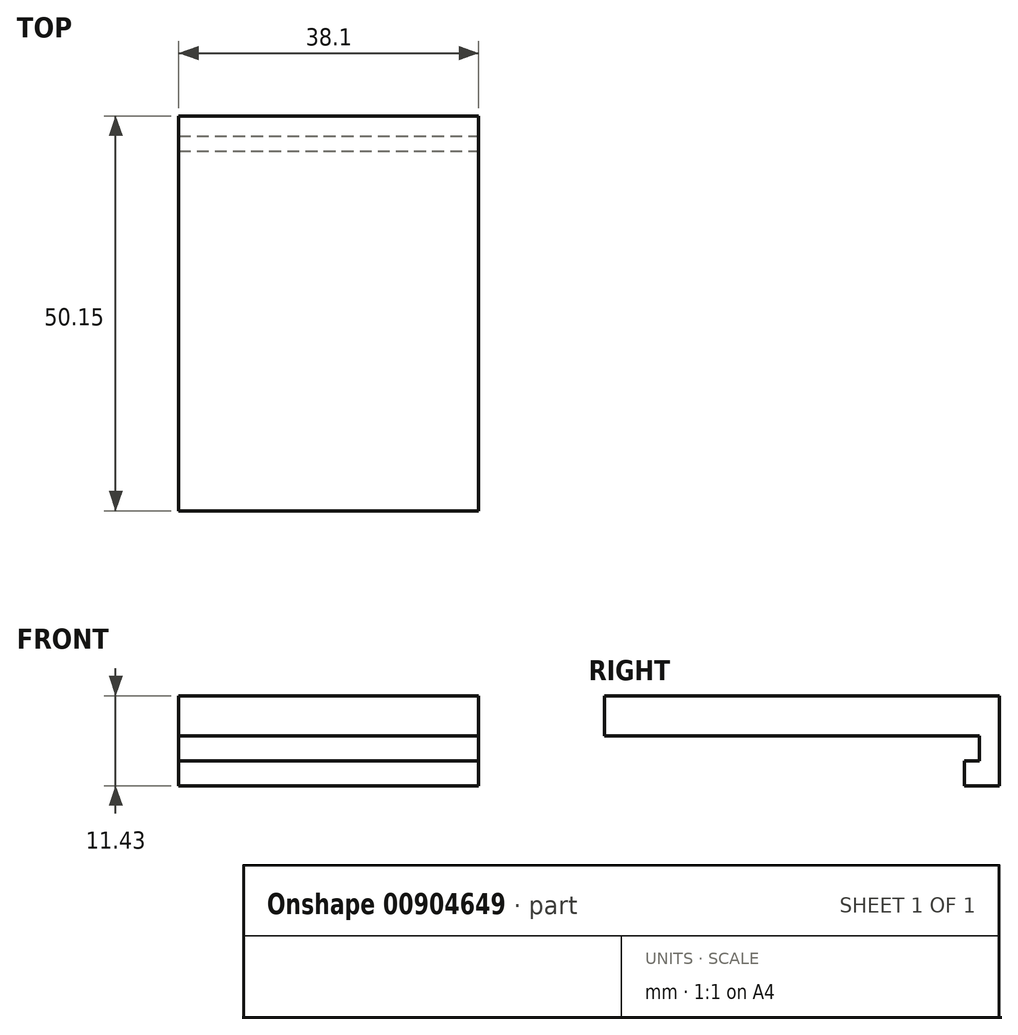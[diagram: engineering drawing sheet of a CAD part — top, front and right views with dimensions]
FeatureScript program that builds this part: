
annotation { "Feature Type Name" : "Feature", "Feature Type Description" : "" }
export const myFeature = defineFeature(function(context is Context, id is Id, definition is map)
    precondition{}
    {
        {
            var Q0;
            Q0=qCreatedBy(makeId("Top.planeOp"),FACE);
            var sketch = newSketch(context, id + "F0", { "sketchPlane" : qUnion([Q0])});
            skLineSegment(sketch, "E0.bottom", {"start": v(19.05, 12.7) * mm, "end": v(-19.05, 12.7) * mm});
            skLineSegment(sketch, "E0.top", {"start": v(19.05, -12.7) * mm, "end": v(-19.05, -12.7) * mm});
            skLineSegment(sketch, "E0.left", {"start": v(19.05, 12.7) * mm, "end": v(19.05, -12.7) * mm});
            skLineSegment(sketch, "E0.right", {"start": v(-19.05, 12.7) * mm, "end": v(-19.05, -12.7) * mm});
            skPoint(sketch, "E0.middle", {"position": v(0, 0) * mm});
            skSolve(sketch);
        }
        {
            var Q0;
            Q0=makeQuery(id+"F0.imprint","IMPRINT",FACE,{"disambiguationData":[TD([[makeQuery(id+"F0.imprint","IMPRINT",EDGE,{"derivedFrom":sQuery(id+"F0.wireOp",EDGE,"E0.bottom")}),1.0]])]});
            extrude(context, id + "F1", {"entities" : qUnion([Q0]), "depth" : 5.08 * mm, "offsetDistance" : 25.4 * mm});
        }
        {
            var Q0;
            Q0=makeQuery(id+"F1.opExtrude","SWEPT_FACE",FACE,{"disambiguationData":[OSD([sQuery(id+"F0.wireOp",EDGE,"E0.bottom")])]});
            var sketch = newSketch(context, id + "F2", { "sketchPlane" : qUnion([Q0])});
            skLineSegment(sketch, "E1.bottom", {"start": v(-19.05, 5.08) * mm, "end": v(19.05, 5.08) * mm});
            skLineSegment(sketch, "E1.top", {"start": v(-19.05, 0) * mm, "end": v(19.05, 0) * mm});
            skLineSegment(sketch, "E1.left", {"start": v(-19.05, 5.08) * mm, "end": v(-19.05, 0) * mm});
            skLineSegment(sketch, "E1.right", {"start": v(19.05, 5.08) * mm, "end": v(19.05, 0) * mm});
            skSolve(sketch);
        }
        {
            var Q0;
            Q0=makeQuery(id+"F2.imprint","IMPRINT",FACE,{"disambiguationData":[TD([[makeQuery(id+"F2.imprint","IMPRINT",EDGE,{"derivedFrom":sQuery(id+"F2.wireOp",EDGE,"E1.bottom")}),-1.0]])]});
            extrude(context, id + "F3", {"entities" : qUnion([Q0]), "operationType" : NewBodyOperationType.ADD, "depth" : 22.22 * mm, "offsetDistance" : 25.4 * mm});
        }
        {
            var Q0;
            Q0=makeQuery(id+"F3.boolean.opBoolean","MERGE",FACE,{"derivedFrom":[makeQuery(id+"F1.opExtrude","SWEPT_FACE",FACE,{"disambiguationData":[OSD([sQuery(id+"F0.wireOp",EDGE,"E0.right")])]}),makeQuery(id+"F3.opExtrude","SWEPT_FACE",FACE,{"disambiguationData":[OSD([sQuery(id+"F2.wireOp",EDGE,"E1.right")])]})]});
            var sketch = newSketch(context, id + "F4", { "sketchPlane" : qUnion([Q0])});
            skLineSegment(sketch, "E2", {"start": v(-34.92, 5.08) * mm, "end": v(-37.45, 5.08) * mm});
            skLineSegment(sketch, "E3", {"start": v(-34.92, 0) * mm, "end": v(-37.45, 0) * mm});
            skLineSegment(sketch, "E4", {"start": v(-37.45, 0) * mm, "end": v(-37.45, 5.08) * mm});
            skSolve(sketch);
        }
        {
            var Q0;
            Q0=makeQuery(id+"F4.imprint","IMPRINT",FACE,{"disambiguationData":[TD([[makeQuery(id+"F4.imprint","IMPRINT",EDGE,{"derivedFrom":sQuery(id+"F4.wireOp",EDGE,"E2")}),1.0]])]});
            extrude(context, id + "F5", {"entities" : qUnion([Q0]), "operationType" : NewBodyOperationType.ADD, "depth" : -38.1 * mm, "offsetDistance" : 25.4 * mm});
        }
        {
            var Q0;
            Q0=makeQuery(id+"F5.boolean.opBoolean","MERGE",FACE,{"derivedFrom":[makeQuery(id+"F3.opExtrude","SWEPT_FACE",FACE,{"disambiguationData":[OSD([sQuery(id+"F2.wireOp",EDGE,"E1.top")])]}),makeQuery(id+"F5.opExtrude","SWEPT_FACE",FACE,{"disambiguationData":[OSD([sQuery(id+"F4.wireOp",EDGE,"E3")])]})]});
            var sketch = newSketch(context, id + "F6", { "sketchPlane" : qUnion([Q0])});
            skLineSegment(sketch, "E5.bottom", {"start": v(-19.05, -37.45) * mm, "end": v(19.05, -37.45) * mm});
            skLineSegment(sketch, "E5.top", {"start": v(-19.05, -34.91) * mm, "end": v(19.05, -34.91) * mm});
            skLineSegment(sketch, "E5.left", {"start": v(-19.05, -37.45) * mm, "end": v(-19.05, -34.91) * mm});
            skLineSegment(sketch, "E5.right", {"start": v(19.05, -37.45) * mm, "end": v(19.05, -34.91) * mm});
            skSolve(sketch);
        }
        {
            var Q0;
            Q0=makeQuery(id+"F6.imprint","IMPRINT",FACE,{"disambiguationData":[TD([[makeQuery(id+"F6.imprint","IMPRINT",EDGE,{"derivedFrom":sQuery(id+"F6.wireOp",EDGE,"E5.bottom")}),-1.0]])]});
            extrude(context, id + "F7", {"entities" : qUnion([Q0]), "operationType" : NewBodyOperationType.ADD, "depth" : 6.35 * mm, "offsetDistance" : 25.4 * mm});
        }
        {
            var Q0;
            Q0=makeQuery(id+"F7.opExtrude","SWEPT_FACE",FACE,{"disambiguationData":[OSD([sQuery(id+"F6.wireOp",EDGE,"E5.top")])]});
            var sketch = newSketch(context, id + "F8", { "sketchPlane" : qUnion([Q0])});
            skLineSegment(sketch, "E6.bottom", {"start": v(-19.05, -6.35) * mm, "end": v(19.05, -6.35) * mm});
            skLineSegment(sketch, "E6.top", {"start": v(-19.05, -3.17) * mm, "end": v(19.05, -3.17) * mm});
            skLineSegment(sketch, "E6.left", {"start": v(19.05, -3.17) * mm, "end": v(19.05, -6.35) * mm});
            skLineSegment(sketch, "E6.right", {"start": v(-19.05, -3.17) * mm, "end": v(-19.05, -6.35) * mm});
            skSolve(sketch);
        }
        {
            var Q0;
            Q0=makeQuery(id+"F8.imprint","IMPRINT",FACE,{"disambiguationData":[TD([[makeQuery(id+"F8.imprint","IMPRINT",EDGE,{"derivedFrom":sQuery(id+"F8.wireOp",EDGE,"E6.bottom")}),1.0]])]});
            extrude(context, id + "F9", {"entities" : qUnion([Q0]), "operationType" : NewBodyOperationType.ADD, "depth" : 1.9 * mm, "offsetDistance" : 25.4 * mm});
        }
    });
